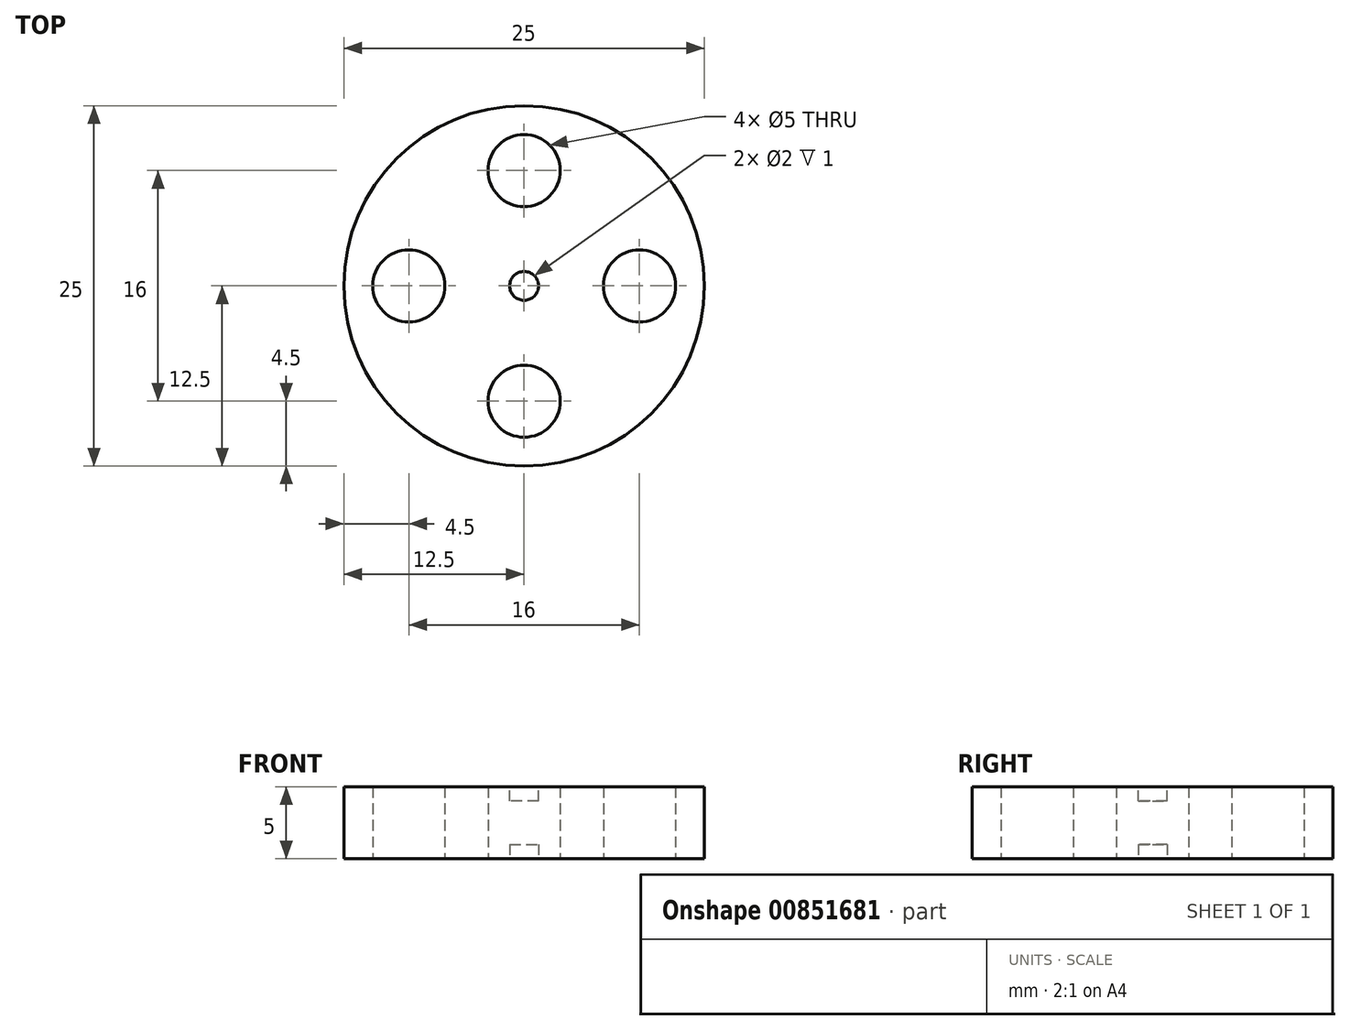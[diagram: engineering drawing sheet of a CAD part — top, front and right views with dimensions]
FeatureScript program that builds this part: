
annotation { "Feature Type Name" : "Feature", "Feature Type Description" : "" }
export const myFeature = defineFeature(function(context is Context, id is Id, definition is map)
    precondition{}
    {
        {
            var Q0;
            Q0=qCreatedBy(makeId("Top.planeOp"),FACE);
            var sketch = newSketch(context, id + "F0", { "sketchPlane" : qUnion([Q0])});
            skCircle(sketch, "E0", {"center": v(0, 0) * mm, "radius": 12.5 * mm});
            skLineSegment(sketch, "E1", {"start": v(0, 0) * mm, "end": v(0, 8) * mm, "construction": true});
            skCircle(sketch, "E2", {"center": v(0, 8) * mm, "radius": 2.5 * mm});
            skLineSegment(sketch, "E3", {"start": v(0, 0) * mm, "end": v(-8, 0) * mm, "construction": true});
            skCircle(sketch, "E4", {"center": v(-8, 0) * mm, "radius": 2.5 * mm});
            skCircle(sketch, "E5.MirrorC", {"center": v(8, 0) * mm, "radius": 2.5 * mm});
            skCircle(sketch, "E6.MirrorC", {"center": v(0, -8) * mm, "radius": 2.5 * mm});
            skSolve(sketch);
        }
        {
            var Q0;
            Q0=makeQuery(id+"F0.imprint","IMPRINT",FACE,{"disambiguationData":[TD([[makeQuery(id+"F0.imprint","IMPRINT",EDGE,{"derivedFrom":sQuery(id+"F0.wireOp",EDGE,"E0")}),1.0]])]});
            extrude(context, id + "F1", {"entities" : qUnion([Q0]), "depth" : 5 * mm, "offsetDistance" : 25 * mm});
        }
        {
            var Q0;
            Q0=makeQuery(id+"F1.opExtrude","CAP_FACE",FACE,{"disambiguationData":[OSD([sQuery(id+"F0.wireOp",EDGE,"E0"),sQuery(id+"F0.wireOp",EDGE,"E2"),sQuery(id+"F0.wireOp",EDGE,"E4")])],"isStart":false});
            var sketch = newSketch(context, id + "F2", { "sketchPlane" : qUnion([Q0])});
            skCircle(sketch, "E7", {"center": v(0, 0) * mm, "radius": 1 * mm});
            skSolve(sketch);
        }
        {
            var Q0;
            Q0=makeQuery(id+"F2.imprint","IMPRINT",FACE,{"disambiguationData":[TD([[makeQuery(id+"F2.imprint","IMPRINT",EDGE,{"derivedFrom":sQuery(id+"F2.wireOp",EDGE,"E7")}),1.0]])]});
            extrude(context, id + "F3", {"entities" : qUnion([Q0]), "operationType" : NewBodyOperationType.REMOVE, "oppositeDirection" : true, "depth" : 1 * mm, "offsetDistance" : 25 * mm});
        }
        {
            var Q0;
            Q0=makeQuery(id+"F1.opExtrude","CAP_FACE",FACE,{"disambiguationData":[OSD([sQuery(id+"F0.wireOp",EDGE,"E0"),sQuery(id+"F0.wireOp",EDGE,"E2"),sQuery(id+"F0.wireOp",EDGE,"E4")])],"isStart":true});
            var sketch = newSketch(context, id + "F4", { "sketchPlane" : qUnion([Q0])});
            skCircle(sketch, "E8", {"center": v(0, 0) * mm, "radius": 1 * mm});
            skSolve(sketch);
        }
        {
            var Q0;
            Q0=makeQuery(id+"F4.imprint","IMPRINT",FACE,{"disambiguationData":[TD([[makeQuery(id+"F4.imprint","IMPRINT",EDGE,{"derivedFrom":sQuery(id+"F4.wireOp",EDGE,"E8")}),1.0]])]});
            extrude(context, id + "F5", {"entities" : qUnion([Q0]), "operationType" : NewBodyOperationType.REMOVE, "oppositeDirection" : true, "depth" : 1 * mm, "offsetDistance" : 25 * mm});
        }
    });
